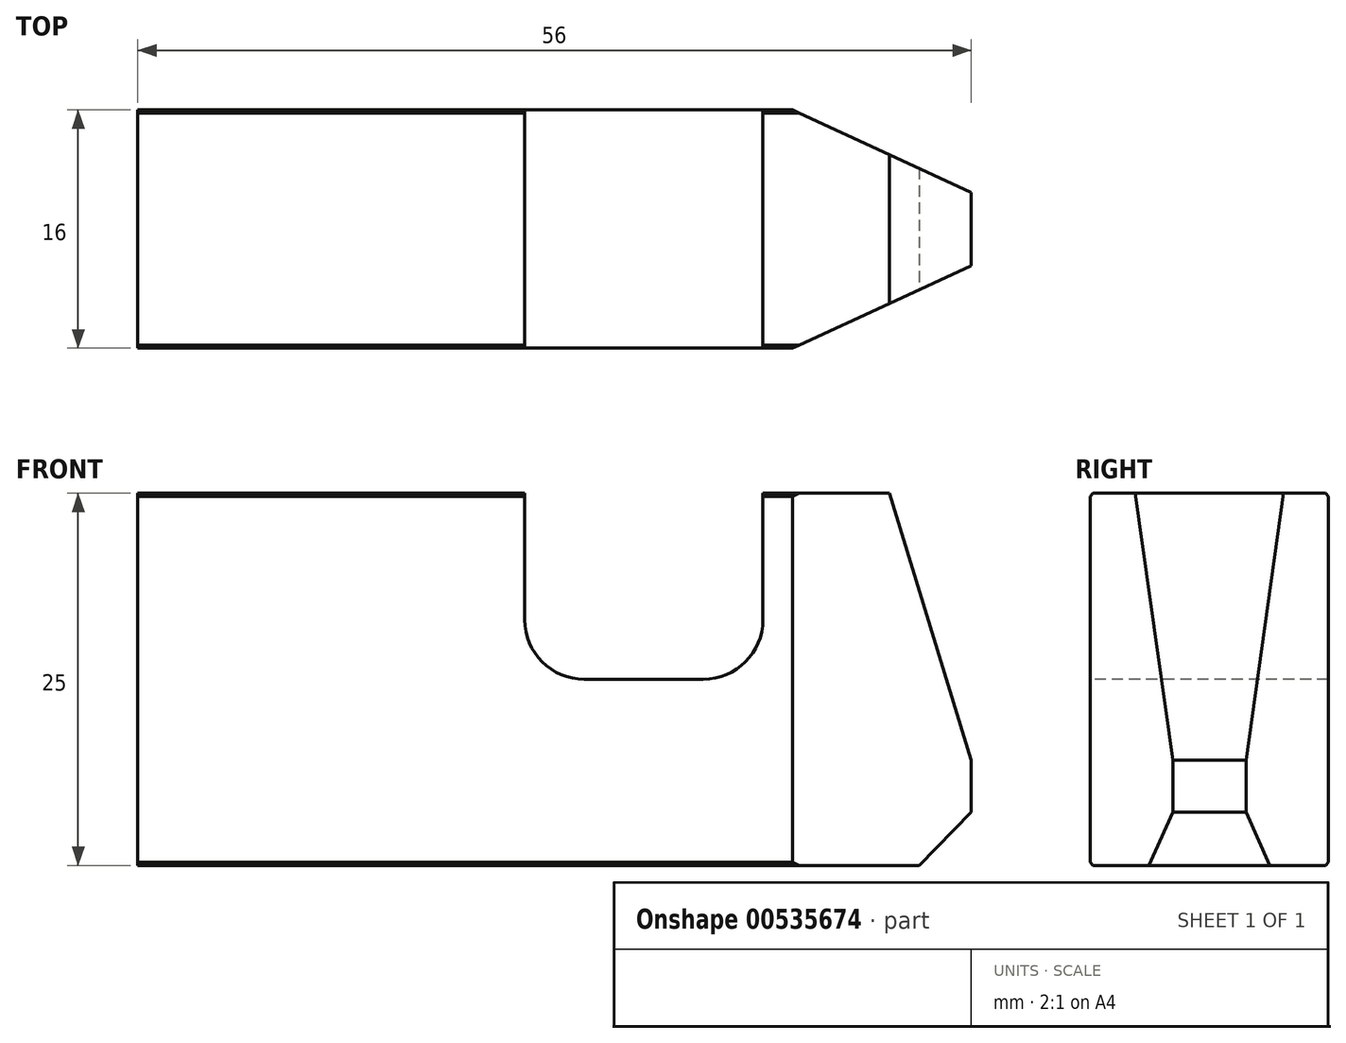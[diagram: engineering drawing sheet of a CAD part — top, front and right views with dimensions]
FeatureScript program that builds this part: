
annotation { "Feature Type Name" : "Feature", "Feature Type Description" : "" }
export const myFeature = defineFeature(function(context is Context, id is Id, definition is map)
    precondition{}
    {
        {
            var Q0;
            Q0=qCreatedBy(makeId("Top.planeOp"),FACE);
            var sketch = newSketch(context, id + "F0", { "sketchPlane" : qUnion([Q0])});
            skLineSegment(sketch, "E0.bottom", {"start": v(-31.4, 7.47) * mm, "end": v(24.6, 7.47) * mm});
            skLineSegment(sketch, "E0.top", {"start": v(-31.4, -8.53) * mm, "end": v(24.6, -8.53) * mm});
            skLineSegment(sketch, "E0.left", {"start": v(-31.4, 7.47) * mm, "end": v(-31.4, -8.53) * mm});
            skLineSegment(sketch, "E0.right", {"start": v(24.6, 7.47) * mm, "end": v(24.6, -8.53) * mm});
            skSolve(sketch);
        }
        {
            var Q0;
            Q0 = qSketchRegion(id + "F0", true);
            extrude(context, id + "F1", {"entities" : qUnion([Q0]), "depth" : 25 * mm, "offsetDistance" : 25 * mm});
        }
        {
            var Q0;
            Q0=makeQuery(id+"F1.opExtrude","CAP_FACE",FACE,{"disambiguationData":[OSD([sQuery(id+"F0.wireOp",EDGE,"E0.bottom"),sQuery(id+"F0.wireOp",EDGE,"E0.top"),sQuery(id+"F0.wireOp",EDGE,"E0.left"),sQuery(id+"F0.wireOp",EDGE,"E0.right")])],"isStart":false});
            var sketch = newSketch(context, id + "F2", { "sketchPlane" : qUnion([Q0])});
            skLineSegment(sketch, "E1", {"start": v(-5.4, 7.47) * mm, "end": v(-5.4, -8.53) * mm});
            skLineSegment(sketch, "E2", {"start": v(10.6, 7.47) * mm, "end": v(10.6, -8.53) * mm});
            skSolve(sketch);
        }
        {
            var Q0;
            {var subQ0=sQuery(id+"F2.wireOp",EDGE,"E1");Q0=makeQuery(id+"F2.imprint","IMPRINT",FACE,{"disambiguationData":[TD([[makeQuery(id+"F2.imprint","IMPRINT",EDGE,{"derivedFrom":subQ0}),1.0]])]});}
            extrude(context, id + "F3", {"entities" : qUnion([Q0]), "operationType" : NewBodyOperationType.REMOVE, "oppositeDirection" : true, "depth" : 12.5 * mm, "offsetDistance" : 25 * mm});
        }
        {
            var Q0;
            Q0=makeQuery(id+"F3.boolean.opBoolean","COPY",EDGE,{"derivedFrom":makeQuery(id+"F3.opExtrude","CAP_EDGE",EDGE,{"disambiguationData":[OSD([sQuery(id+"F2.wireOp",EDGE,"E2")])],"isStart":false})});
            var Q1;
            Q1=makeQuery(id+"F3.boolean.opBoolean","COPY",EDGE,{"derivedFrom":makeQuery(id+"F3.opExtrude","CAP_EDGE",EDGE,{"disambiguationData":[OSD([sQuery(id+"F2.wireOp",EDGE,"E1")])],"isStart":false})});
            fillet(context, id + "F4", {"entities" : qUnion([Q0, Q1]), "radius" : 4 * mm, "tangentPropagation" : true, "allowEdgeOverflow" : false});
        }
        {
            var Q0;
            {var subQ0=sQuery(id+"F0.wireOp",EDGE,"E0.bottom");var subQ1=sQuery(id+"F0.wireOp",EDGE,"E0.right");var subQ2=sQuery(id+"F0.wireOp",EDGE,"E0.top");Q0=makeQuery(id+"F3.boolean.opBoolean","SPLIT",FACE,{"disambiguationData":[TD([makeQuery(id+"F1.opExtrude","SWEPT_FACE",FACE,{"disambiguationData":[OSD([subQ1])]})])],"derivedFrom":makeQuery(id+"F1.opExtrude","CAP_FACE",FACE,{"disambiguationData":[OSD([subQ0,subQ2,sQuery(id+"F0.wireOp",EDGE,"E0.left"),subQ1])],"isStart":false})});}
            var sketch = newSketch(context, id + "F5", { "sketchPlane" : qUnion([Q0])});
            skLineSegment(sketch, "E3", {"start": v(12.6, 7.47) * mm, "end": v(19.1, 4.47) * mm});
            skLineSegment(sketch, "E4", {"start": v(12.6, -8.53) * mm, "end": v(19.1, -5.53) * mm});
            skLineSegment(sketch, "E5", {"start": v(19.1, 4.47) * mm, "end": v(19.1, 7.47) * mm});
            skLineSegment(sketch, "E6", {"start": v(19.1, -5.53) * mm, "end": v(19.1, -8.53) * mm});
            skLineSegment(sketch, "E7", {"start": v(19.1, -5.53) * mm, "end": v(24.6, -3) * mm});
            skLineSegment(sketch, "E8", {"start": v(19.1, 4.47) * mm, "end": v(24.6, 1.93) * mm});
            skSolve(sketch);
        }
        {
            var Q0;
            Q0=makeQuery(id+"F1.opExtrude","SWEPT_FACE",FACE,{"disambiguationData":[OSD([sQuery(id+"F0.wireOp",EDGE,"E0.top")])]});
            var sketch = newSketch(context, id + "F6", { "sketchPlane" : qUnion([Q0])});
            skLineSegment(sketch, "E9", {"start": v(19.1, 25) * mm, "end": v(24.6, 7.07) * mm});
            skLineSegment(sketch, "E10", {"start": v(24.6, 3.57) * mm, "end": v(21.1, 0) * mm});
            skSolve(sketch);
        }
        {
            var Q0;
            {var subQ0=sQuery(id+"F6.wireOp",EDGE,"E9");Q0=makeQuery(id+"F6.imprint","IMPRINT",FACE,{"disambiguationData":[TD([[makeQuery(id+"F6.imprint","IMPRINT",EDGE,{"derivedFrom":subQ0}),1.0]])]});}
            var Q1;
            {var subQ0=sQuery(id+"F6.wireOp",EDGE,"E10");Q1=makeQuery(id+"F6.imprint","IMPRINT",FACE,{"disambiguationData":[TD([[makeQuery(id+"F6.imprint","IMPRINT",EDGE,{"derivedFrom":subQ0}),1.0]])]});}
            extrude(context, id + "F7", {"entities" : qUnion([Q0, Q1]), "operationType" : NewBodyOperationType.REMOVE, "oppositeDirection" : true, "depth" : 25 * mm, "offsetDistance" : 25 * mm});
        }
        {
            var Q0;
            {var subQ0=sQuery(id+"F5.wireOp",EDGE,"E3");Q0=makeQuery(id+"F5.imprint","IMPRINT",FACE,{"disambiguationData":[TD([[makeQuery(id+"F5.imprint","IMPRINT",EDGE,{"derivedFrom":subQ0}),1.0]])]});}
            var Q1;
            {var subQ0=sQuery(id+"F5.wireOp",EDGE,"E4");Q1=makeQuery(id+"F5.imprint","IMPRINT",FACE,{"disambiguationData":[TD([[makeQuery(id+"F5.imprint","IMPRINT",EDGE,{"derivedFrom":subQ0}),-1.0]])]});}
            var Q2;
            {var subQ0=sQuery(id+"F5.wireOp",EDGE,"E5");Q2=makeQuery(id+"F5.imprint","IMPRINT",FACE,{"disambiguationData":[TD([[makeQuery(id+"F5.imprint","IMPRINT",EDGE,{"derivedFrom":subQ0}),-1.0]])]});}
            var Q3;
            {var subQ0=sQuery(id+"F5.wireOp",EDGE,"E6");Q3=makeQuery(id+"F5.imprint","IMPRINT",FACE,{"disambiguationData":[TD([[makeQuery(id+"F5.imprint","IMPRINT",EDGE,{"derivedFrom":subQ0}),1.0]])]});}
            extrude(context, id + "F8", {"entities" : qUnion([Q0, Q1, Q2, Q3]), "operationType" : NewBodyOperationType.REMOVE, "oppositeDirection" : true, "depth" : 25 * mm, "offsetDistance" : 25 * mm});
        }
        {
            var Q0;
            {var subQ0=sQuery(id+"F0.wireOp",EDGE,"E0.left");var subQ1=sQuery(id+"F0.wireOp",EDGE,"E0.top");Q0=makeQuery(id+"F3.boolean.opBoolean","SPLIT",EDGE,{"disambiguationData":[TD([makeQuery(id+"F1.opExtrude","SWEPT_FACE",FACE,{"disambiguationData":[OSD([subQ0])]})])],"derivedFrom":makeQuery(id+"F1.opExtrude","CAP_EDGE",EDGE,{"disambiguationData":[OSD([subQ1])],"isStart":false})});}
            var Q1;
            {var subQ0=sQuery(id+"F0.wireOp",EDGE,"E0.bottom");var subQ1=sQuery(id+"F0.wireOp",EDGE,"E0.left");Q1=makeQuery(id+"F3.boolean.opBoolean","SPLIT",EDGE,{"disambiguationData":[TD([makeQuery(id+"F1.opExtrude","SWEPT_FACE",FACE,{"disambiguationData":[OSD([subQ1])]})])],"derivedFrom":makeQuery(id+"F1.opExtrude","CAP_EDGE",EDGE,{"disambiguationData":[OSD([subQ0])],"isStart":false})});}
            var Q2;
            {var subQ0=sQuery(id+"F0.wireOp",EDGE,"E0.bottom");var subQ1=sQuery(id+"F0.wireOp",EDGE,"E0.right");Q2=makeQuery(id+"F3.boolean.opBoolean","SPLIT",EDGE,{"disambiguationData":[TD([makeQuery(id+"F1.opExtrude","SWEPT_FACE",FACE,{"disambiguationData":[OSD([subQ1])]})])],"derivedFrom":makeQuery(id+"F1.opExtrude","CAP_EDGE",EDGE,{"disambiguationData":[OSD([subQ0])],"isStart":false})});}
            var Q3;
            {var subQ0=sQuery(id+"F0.wireOp",EDGE,"E0.right");var subQ1=sQuery(id+"F0.wireOp",EDGE,"E0.top");Q3=makeQuery(id+"F3.boolean.opBoolean","SPLIT",EDGE,{"disambiguationData":[TD([makeQuery(id+"F1.opExtrude","SWEPT_FACE",FACE,{"disambiguationData":[OSD([subQ0])]})])],"derivedFrom":makeQuery(id+"F1.opExtrude","CAP_EDGE",EDGE,{"disambiguationData":[OSD([subQ1])],"isStart":false})});}
            var Q4;
            Q4=makeQuery(id+"F1.opExtrude","CAP_EDGE",EDGE,{"disambiguationData":[OSD([sQuery(id+"F0.wireOp",EDGE,"E0.top")])],"isStart":true});
            var Q5;
            Q5=makeQuery(id+"F1.opExtrude","CAP_EDGE",EDGE,{"disambiguationData":[OSD([sQuery(id+"F0.wireOp",EDGE,"E0.bottom")])],"isStart":true});
            chamfer(context, id + "F9", {"entities" : qUnion([Q0, Q1, Q2, Q3, Q4, Q5]), "width" : .2 * mm, "tangentPropagation" : true});
        }
    });
